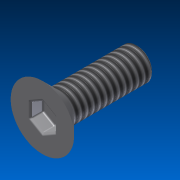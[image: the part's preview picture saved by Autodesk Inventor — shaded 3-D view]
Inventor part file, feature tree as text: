
AUTODESK INVENTOR PART (.ipt)
format: ipt  version: 2013 (Build 170138000, 138)  size: 167,424 bytes
history: native  units: mm
features: sketch x3, extrude x2, other x1, revolve x1, chamfer x1, fillet x1, thread x1
ambient origin geometry x1: Origin
feature tree (10):
  other  "ソリッド1"
  revolve  "回転1"
  extrude  "押し出し1"  TaperAngle=45.0deg  [1 undecoded]
  extrude  "押し出し2"  Depth=2.0mm
  chamfer  "面取り1"  Distance=1.0mm
  fillet  "フィレット1"  [1 undecoded]
  thread  "ねじ1"
  sketch  "スケッチ1"
  sketch  "スケッチ2"
  sketch  "スケッチ3"
note: 2 required parameter values undecoded (feature->parameter linkage not recoverable at this tier; creation-order binding heuristic only, values carry confidence <= 0.55)
